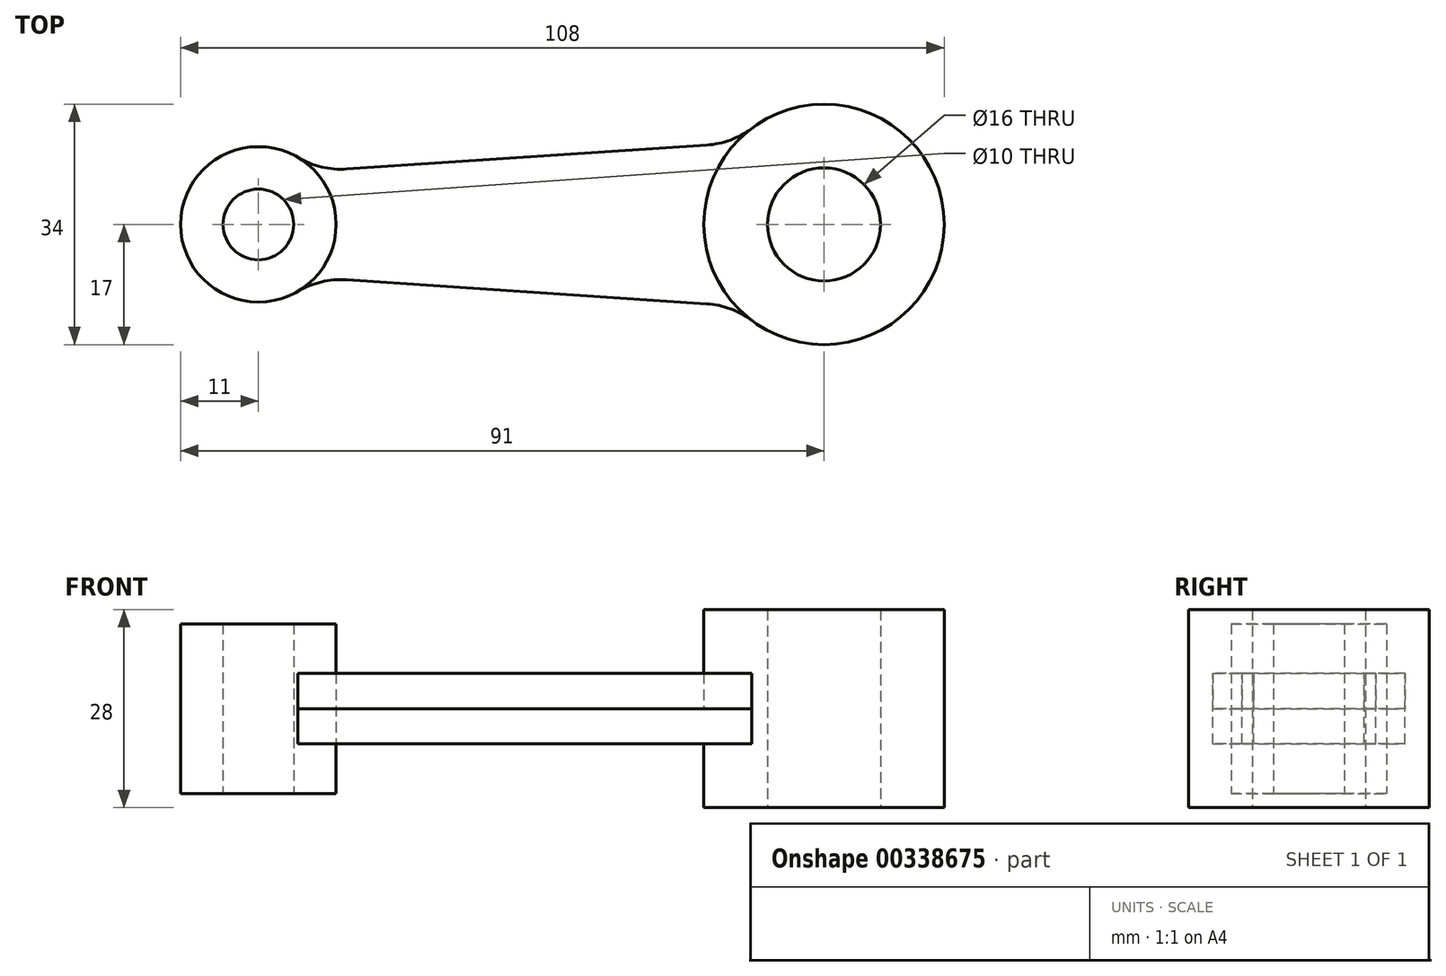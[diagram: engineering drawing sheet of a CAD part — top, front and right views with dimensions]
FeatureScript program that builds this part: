
annotation { "Feature Type Name" : "Feature", "Feature Type Description" : "" }
export const myFeature = defineFeature(function(context is Context, id is Id, definition is map)
    precondition{}
    {
        {
            var Q0;
            Q0=qCreatedBy(makeId("Top.planeOp"),FACE);
            var sketch = newSketch(context, id + "F0", { "sketchPlane" : qUnion([Q0])});
            skArc(sketch, "E0", {"start": v(5.6, 9.47) * mm, "mid": v(-11, 0) * mm, "end": v(5.6, -9.47) * mm});
            skCircle(sketch, "E1", {"center": v(0, 0) * mm, "radius": 5 * mm});
            skArc(sketch, "E2", {"start": v(69.8, -13.6) * mm, "mid": v(97, 0) * mm, "end": v(69.8, 13.6) * mm});
            skCircle(sketch, "E3", {"center": v(80, 0) * mm, "radius": 8 * mm});
            skLineSegment(sketch, "E4", {"start": v(60, -11) * mm, "end": v(15, -8) * mm});
            skLineSegment(sketch, "E5", {"start": v(15, 8) * mm, "end": v(60, 11) * mm});
            skLineSegment(sketch, "E6", {"start": v(15, 8) * mm, "end": v(12.5, 7.83) * mm});
            skLineSegment(sketch, "E7", {"start": v(15, -8) * mm, "end": v(12.5, -7.83) * mm});
            skLineSegment(sketch, "E8", {"start": v(60, -11) * mm, "end": v(63.4, -11.23) * mm});
            skLineSegment(sketch, "E9", {"start": v(60, 11) * mm, "end": v(63.4, 11.23) * mm});
            skPoint(sketch, "E10.visualSharp", {"position": v(67.48, 11.5) * mm});
            skArc(sketch, "E10.filletArc", {"start": v(63.4, 11.23) * mm, "mid": v(66.77, 11.95) * mm, "end": v(69.8, 13.6) * mm});
            skPoint(sketch, "E11.visualSharp", {"position": v(67.48, -11.5) * mm});
            skArc(sketch, "E11.filletArc", {"start": v(69.8, -13.6) * mm, "mid": v(66.77, -11.95) * mm, "end": v(63.4, -11.23) * mm});
            skPoint(sketch, "E12.visualSharp", {"position": v(8.01, 7.53) * mm});
            skArc(sketch, "E12.filletArc", {"start": v(5.6, 9.47) * mm, "mid": v(8.92, 8.13) * mm, "end": v(12.5, 7.83) * mm});
            skPoint(sketch, "E13.visualSharp", {"position": v(8.01, -7.53) * mm});
            skArc(sketch, "E13.filletArc", {"start": v(12.5, -7.83) * mm, "mid": v(8.92, -8.13) * mm, "end": v(5.6, -9.47) * mm});
            skCircle(sketch, "E14", {"center": v(0, 0) * mm, "radius": 11 * mm});
            skCircle(sketch, "E15", {"center": v(80, 0) * mm, "radius": 17 * mm});
            skSolve(sketch);
        }
        {
            var Q0;
            Q0=makeQuery(id+"F0.imprint","IMPRINT",FACE,{"disambiguationData":[TD([[makeQuery(id+"F0.imprint","IMPRINT",EDGE,{"derivedFrom":sQuery(id+"F0.wireOp",EDGE,"E1")}),-1.0]])]});
            extrude(context, id + "F1", {"entities" : qUnion([Q0]), "depth" : 12 * mm});
        }
        {
            var Q0;
            Q0=makeQuery(id+"F1.opExtrude","CAP_FACE",FACE,{"disambiguationData":[OSD([sQuery(id+"F0.wireOp",EDGE,"E1"),sQuery(id+"F0.wireOp",EDGE,"E14")])],"isStart":false});
            extrude(context, id + "F2", {"entities" : qUnion([Q0]), "operationType" : NewBodyOperationType.ADD, "oppositeDirection" : true, "depth" : 24 * mm});
        }
        {
            var Q0;
            Q0=makeQuery(id+"F0.imprint","IMPRINT",FACE,{"disambiguationData":[TD([[makeQuery(id+"F0.imprint","IMPRINT",EDGE,{"derivedFrom":sQuery(id+"F0.wireOp",EDGE,"E3")}),-1.0]])]});
            extrude(context, id + "F3", {"entities" : qUnion([Q0]), "depth" : 14 * mm});
        }
        {
            var Q0;
            Q0=makeQuery(id+"F3.opExtrude","CAP_FACE",FACE,{"disambiguationData":[OSD([sQuery(id+"F0.wireOp",EDGE,"E3"),sQuery(id+"F0.wireOp",EDGE,"E15")])],"isStart":false});
            extrude(context, id + "F4", {"entities" : qUnion([Q0]), "operationType" : NewBodyOperationType.ADD, "oppositeDirection" : true, "depth" : 28 * mm});
        }
        {
            var Q0;
            Q0=makeQuery(id+"F0.imprint","IMPRINT",FACE,{"disambiguationData":[TD([[makeQuery(id+"F0.imprint","IMPRINT",EDGE,{"derivedFrom":sQuery(id+"F0.wireOp",EDGE,"E4")}),-1.0]])]});
            extrude(context, id + "F5", {"entities" : qUnion([Q0]), "depth" : 5 * mm});
        }
        {
            var Q0;
            Q0=makeQuery(id+"F5.opExtrude","CAP_FACE",FACE,{"disambiguationData":[OSD([sQuery(id+"F0.wireOp",EDGE,"E4"),sQuery(id+"F0.wireOp",EDGE,"E5"),sQuery(id+"F0.wireOp",EDGE,"E6"),sQuery(id+"F0.wireOp",EDGE,"E7"),sQuery(id+"F0.wireOp",EDGE,"E8"),sQuery(id+"F0.wireOp",EDGE,"E9"),sQuery(id+"F0.wireOp",EDGE,"E10.filletArc"),sQuery(id+"F0.wireOp",EDGE,"E11.filletArc"),sQuery(id+"F0.wireOp",EDGE,"E12.filletArc"),sQuery(id+"F0.wireOp",EDGE,"E13.filletArc"),sQuery(id+"F0.wireOp",EDGE,"E14"),sQuery(id+"F0.wireOp",EDGE,"E15")])],"isStart":false});
            extrude(context, id + "F6", {"entities" : qUnion([Q0]), "oppositeDirection" : true, "depth" : 10 * mm});
        }
    });
